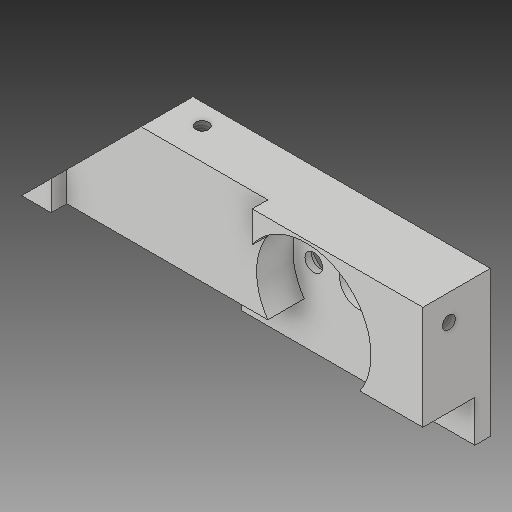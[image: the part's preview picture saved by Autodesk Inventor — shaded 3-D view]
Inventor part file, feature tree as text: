
AUTODESK INVENTOR PART (.ipt)
format: ipt  version: 2019 (Build 230136000, 136)  size: 169,472 bytes
history: native  units: mm
features: sketch x12, other x4
ambient origin geometry x8: Origin, YZ Plane, XZ Plane, XY Plane, X Axis, Y Axis, Z Axis, Center Point
bodies: Body1 (feature_tree)
feature tree (16):
  other  "mocowanie_silnika_wariant1.ipt"
  other  "Solid1::mocowanie_silnika_wariant1.ipt"
  other  "Bryła wyprowadzona1"
  sketch  "Sketch1"  dims[d0=10.0mm]
  sketch  "Sketch2"
  sketch  "Sketch3"
  sketch  "Sketch4"
  sketch  "Sketch6"
  sketch  "Sketch7"
  sketch  "Sketch8"
  sketch  "Sketch9"
  sketch  "Sketch10"
  sketch  "Sketch11"
  sketch  "Sketch12"
  sketch  "Sketch13"
  other  "Bryła1"
